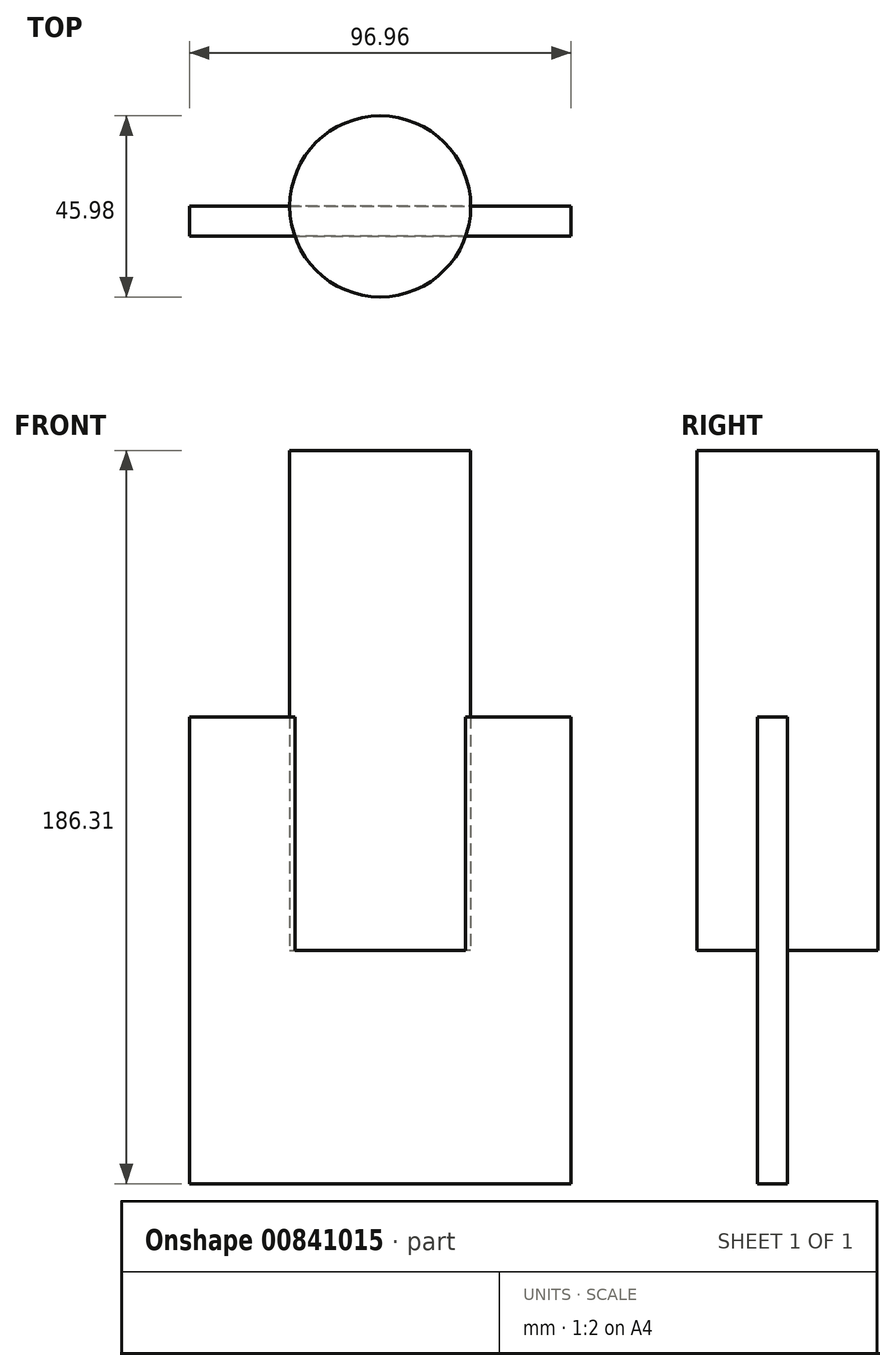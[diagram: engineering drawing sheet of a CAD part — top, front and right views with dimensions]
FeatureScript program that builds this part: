
annotation { "Feature Type Name" : "Feature", "Feature Type Description" : "" }
export const myFeature = defineFeature(function(context is Context, id is Id, definition is map)
    precondition{}
    {
        {
            var Q0;
            Q0=qCreatedBy(makeId("Top.planeOp"),FACE);
            var sketch = newSketch(context, id + "F0", { "sketchPlane" : qUnion([Q0])});
            skCircle(sketch, "E0", {"center": v(0, 0) * mm, "radius": 22.99 * mm});
            skSolve(sketch);
        }
        {
            var Q0;
            Q0 = qSketchRegion(id + "F0", true);
            extrude(context, id + "F1", {"entities" : qUnion([Q0]), "depth" : 127 * mm, "offsetDistance" : 25.4 * mm});
        }
        {
            var Q0;
            Q0=qCreatedBy(makeId("Front.planeOp"),FACE);
            var sketch = newSketch(context, id + "F2", { "sketchPlane" : qUnion([Q0])});
            skLineSegment(sketch, "E1.bottom", {"start": v(48.48, 59.31) * mm, "end": v(-48.48, 59.31) * mm});
            skLineSegment(sketch, "E1.top", {"start": v(48.48, -59.31) * mm, "end": v(-48.48, -59.31) * mm});
            skLineSegment(sketch, "E1.left", {"start": v(48.48, 59.31) * mm, "end": v(48.48, -59.31) * mm});
            skLineSegment(sketch, "E1.right", {"start": v(-48.48, 59.31) * mm, "end": v(-48.48, -59.31) * mm});
            skPoint(sketch, "E1.middle", {"position": v(0, 0) * mm});
            skSolve(sketch);
        }
        {
            var Q0;
            Q0 = qSketchRegion(id + "F2", true);
            extrude(context, id + "F3", {"entities" : qUnion([Q0]), "operationType" : NewBodyOperationType.ADD, "depth" : 7.62 * mm, "offsetDistance" : 25.4 * mm});
        }
    });
